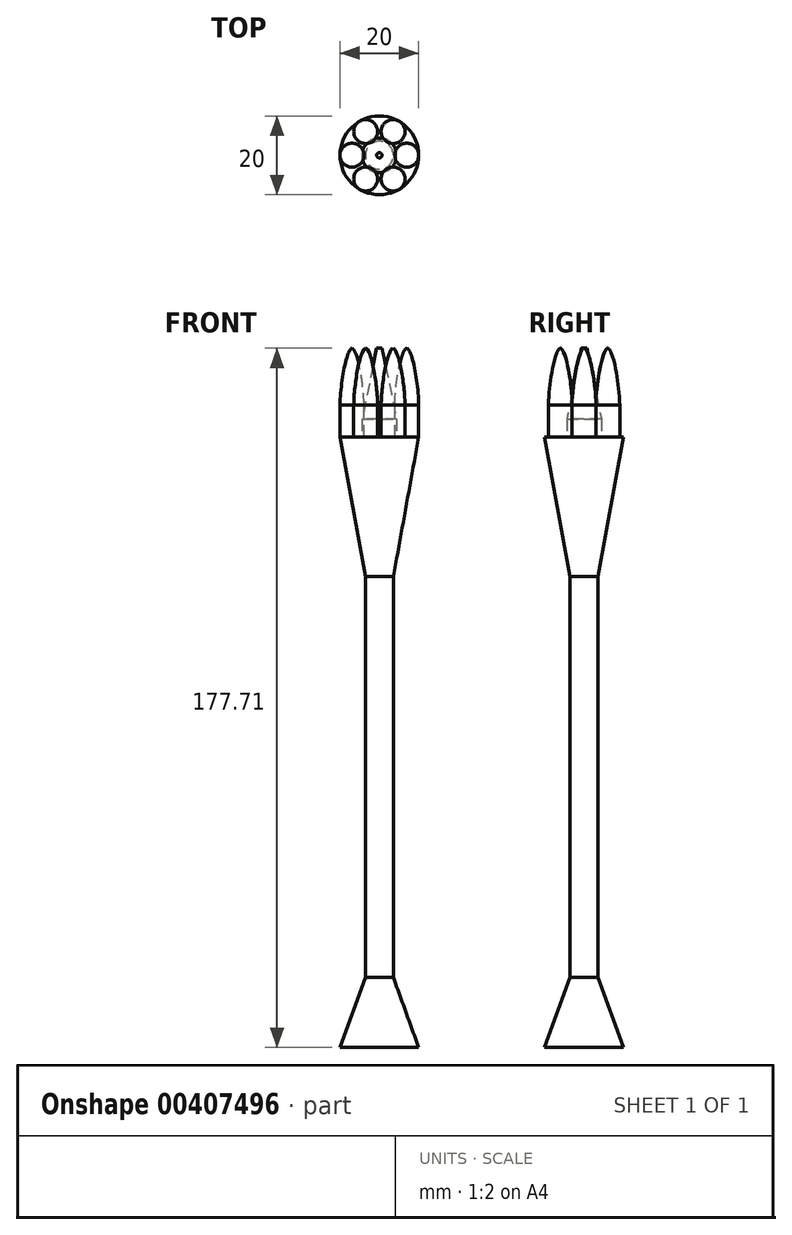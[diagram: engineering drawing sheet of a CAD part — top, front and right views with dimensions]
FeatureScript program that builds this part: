
annotation { "Feature Type Name" : "Feature", "Feature Type Description" : "" }
export const myFeature = defineFeature(function(context is Context, id is Id, definition is map)
    precondition{}
    {
        {
            var Q0;
            Q0=qCreatedBy(makeId("Front.planeOp"),FACE);
            var sketch = newSketch(context, id + "F0", { "sketchPlane" : qUnion([Q0])});
            skLineSegment(sketch, "E0", {"start": v(0, -49.64) * mm, "end": v(-10, -49.64) * mm});
            skLineSegment(sketch, "E1", {"start": v(-3.55, -14.74) * mm, "end": v(-3.55, -31.84) * mm});
            skLineSegment(sketch, "E2", {"start": v(-3.55, -31.84) * mm, "end": v(-10, -49.64) * mm});
            skLineSegment(sketch, "E3", {"start": v(0, -49.64) * mm, "end": v(0, 130.36) * mm, "construction": true});
            skLineSegment(sketch, "E4", {"start": v(-3.55, -14.74) * mm, "end": v(-3.55, 70.04) * mm, "construction": true});
            skLineSegment(sketch, "E5", {"start": v(0, 130.36) * mm, "end": v(-10, 130.36) * mm, "construction": true});
            skLineSegment(sketch, "E6", {"start": v(0, 105.5) * mm, "end": v(-10, 105.5) * mm});
            skLineSegment(sketch, "E7", {"start": v(-10, 105.5) * mm, "end": v(-3.55, 70.04) * mm});
            skLineSegment(sketch, "E8", {"start": v(-3.55, 70.04) * mm, "end": v(-3.55, -31.84) * mm});
            skLineSegment(sketch, "E9", {"start": v(0, 105.5) * mm, "end": v(0, -49.64) * mm});
            skLineSegment(sketch, "E10", {"start": v(0, 33.45) * mm, "end": v(-3.5, 33.45) * mm, "construction": true});
            skSolve(sketch);
        }
        {
            var Q0;
            Q0 = qSketchRegion(id + "F0", true);
            var Q1;
            Q1=sQuery(id+"F0.wireOp",EDGE,"E9");
            revolve(context, id + "F1", {"entities" : qUnion([Q0]), "axis" : qUnion([Q1]), "revolveType" : RevolveType.FULL});
        }
        {
            var Q0;
            Q0=qCreatedBy(makeId("Front.planeOp"),FACE);
            var sketch = newSketch(context, id + "F2", { "sketchPlane" : qUnion([Q0])});
            skLineSegment(sketch, "E11.0", {"start": v(-10, 105.5) * mm, "end": v(10, 105.5) * mm});
            skLineSegment(sketch, "E12", {"start": v(10, 105.5) * mm, "end": v(10, 113.64) * mm});
            skFitSpline(sketch, "E13", {"points": [v(10, 113.64) * mm, v(6.95, 128.07) * mm], "startDerivative": vector(-0.3, 15.84) * mm, "endDerivative": vector(-4.54, 1.56) * mm});
            skLineSegment(sketch, "E14", {"start": v(6.95, 128.07) * mm, "end": v(6.95, 105.5) * mm});
            skSolve(sketch);
        }
        {
            var Q0;
            {var subQ0=sQuery(id+"F2.wireOp",EDGE,"E12");Q0=makeQuery(id+"F2.imprint","IMPRINT",FACE,{"disambiguationData":[TD([[makeQuery(id+"F2.imprint","IMPRINT",EDGE,{"derivedFrom":subQ0}),1.0]])]});}
            var Q1;
            Q1=sQuery(id+"F2.wireOp",EDGE,"E14");
            revolve(context, id + "F3", {"entities" : qUnion([Q0]), "axis" : qUnion([Q1]), "revolveType" : RevolveType.FULL});
        }
        {
            var Q0;
            Q0=makeQuery(id+"F3.opRevolve","SWEPT_BODY",BODY,{"disambiguationData":[OSD([sQuery(id+"F2.wireOp",EDGE,"E11.0"),sQuery(id+"F2.wireOp",EDGE,"E12"),sQuery(id+"F2.wireOp",EDGE,"E13"),sQuery(id+"F2.wireOp",EDGE,"E14")])]});
            var Q1;
            Q1=makeQuery(id+"F1.opRevolve","SWEPT_EDGE",EDGE,{"disambiguationData":[OSD([sQuery(id+"F0.wireOp",EDGE,"E6"),sQuery(id+"F0.wireOp",EDGE,"E7")])]});
            circularPattern(context, id + "F4", {"entities" : qUnion([Q0]), "axis" : qUnion([Q1]), "angle" : 360 * degree, "instanceCount" : 6, "equalSpace" : true});
        }
        {
            var Q0;
            Q0=makeQuery(id+"F1.opRevolve","SWEPT_FACE",FACE,{"disambiguationData":[OSD([sQuery(id+"F0.wireOp",EDGE,"E6")])]});
            var sketch = newSketch(context, id + "F5", { "sketchPlane" : qUnion([Q0])});
            skCircle(sketch, "E15", {"center": v(0, 0) * mm, "radius": 4.39 * mm});
            skSolve(sketch);
        }
        {
            var Q0;
            Q0=makeQuery(id+"F5.imprint","IMPRINT",FACE,{"disambiguationData":[TD([[makeQuery(id+"F5.imprint","IMPRINT",EDGE,{"derivedFrom":sQuery(id+"F5.wireOp",EDGE,"E15")}),1.0]])]});
            extrude(context, id + "F6", {"entities" : qUnion([Q0]), "depth" : 22.53 * mm});
        }
        {
            var Q0;
            Q0=makeQuery(id+"F6.opExtrude","CAP_EDGE",EDGE,{"disambiguationData":[OSD([sQuery(id+"F5.wireOp",EDGE,"E15")])],"isStart":false});
            chamfer(context, id + "F7", {"entities" : qUnion([Q0]), "chamferType" : ChamferType.TWO_OFFSETS, "width1" : 3.7 * mm, "oppositeDirection" : false, "width2" : 18 * mm, "tangentPropagation" : true});
        }
    });
